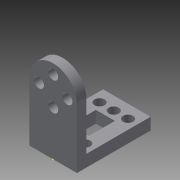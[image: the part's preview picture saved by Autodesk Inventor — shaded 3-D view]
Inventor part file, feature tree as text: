
AUTODESK INVENTOR PART (.ipt)
format: ipt  version: 2015 (Build 190159000, 159)  size: 141,824 bytes
history: native  units: mm
features: sketch x7, extrude x6, pattern_circular x1, pattern_linear x1
ambient origin geometry x8: Origin, YZ Plane, XZ Plane, XY Plane, X Axis, Y Axis, Z Axis, Center Point
bodies: Solid1 (feature_tree)
feature tree (15):
  extrude  "Extrusion1"  Depth=4.0mm TaperAngle=0.0deg
  extrude  "Extrusion2"  Depth=6.0mm
  pattern_circular  "Circular Pattern1"  Count=4 Angle=360.0deg
  extrude  "Extrusion3"  Depth=4.0mm TaperAngle=0.0deg
  extrude  "Extrusion4"  Depth=27.0mm TaperAngle=0.0deg
  sketch  "Sketch5"  dims[d13=5.0mm d14=27.0mm d15=0.0mm]
  extrude  "Extrusion5"  Depth=27.0mm TaperAngle=0.0deg
  pattern_linear  "Rectangular Pattern1"  Count1=3 Spacing1=6.0mm
  extrude  "Extrusion6"  Depth=27.0mm
  sketch  "Sketch1"  dims[d0=20.0mm d1=4.0mm d2=0.0mm]
  sketch  "Sketch2"  dims[d3=6.0mm d4=4.25mm]
  sketch  "Sketch3"  dims[d5=4.0mm d6=0.0mm d7=40.0mm d8=360.0deg]
  sketch  "Sketch4"  dims[d10=25.0mm d11=4.0mm d12=0.0mm]
  sketch  "Sketch6"  dims[d16=6.0mm d18=27.0mm d19=0.0mm d20=30.0mm d22=6.0mm]
  sketch  "Sketch7"  dims[d23=20.0mm d25=18.0mm d26=2.0mm d27=4.25mm d29=8.0mm d30=11.0mm d31=27.0mm d32=0.0mm]
